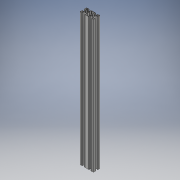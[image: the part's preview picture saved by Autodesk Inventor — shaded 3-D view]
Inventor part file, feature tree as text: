
AUTODESK INVENTOR PART (.ipt)
format: ipt  version: 2018 (Build 220112000, 112)  size: 577,024 bytes
history: native  units: mm
features: other x1, extrude x1, sketch x1
ambient origin geometry x8: Origin, YZ Plane, XZ Plane, XY Plane, X Axis, Y Axis, Z Axis, Center Point
bodies: Body1 (feature_tree)
feature tree (3):
  other  "Sólido1"
  extrude  "Extrusão1"  [1 undecoded]
  sketch  "Esboço1"  dims[d0=585.0mm d1=0.0mm]
note: 1 required parameter value undecoded (feature->parameter linkage not recoverable at this tier; creation-order binding heuristic only, values carry confidence <= 0.55)
